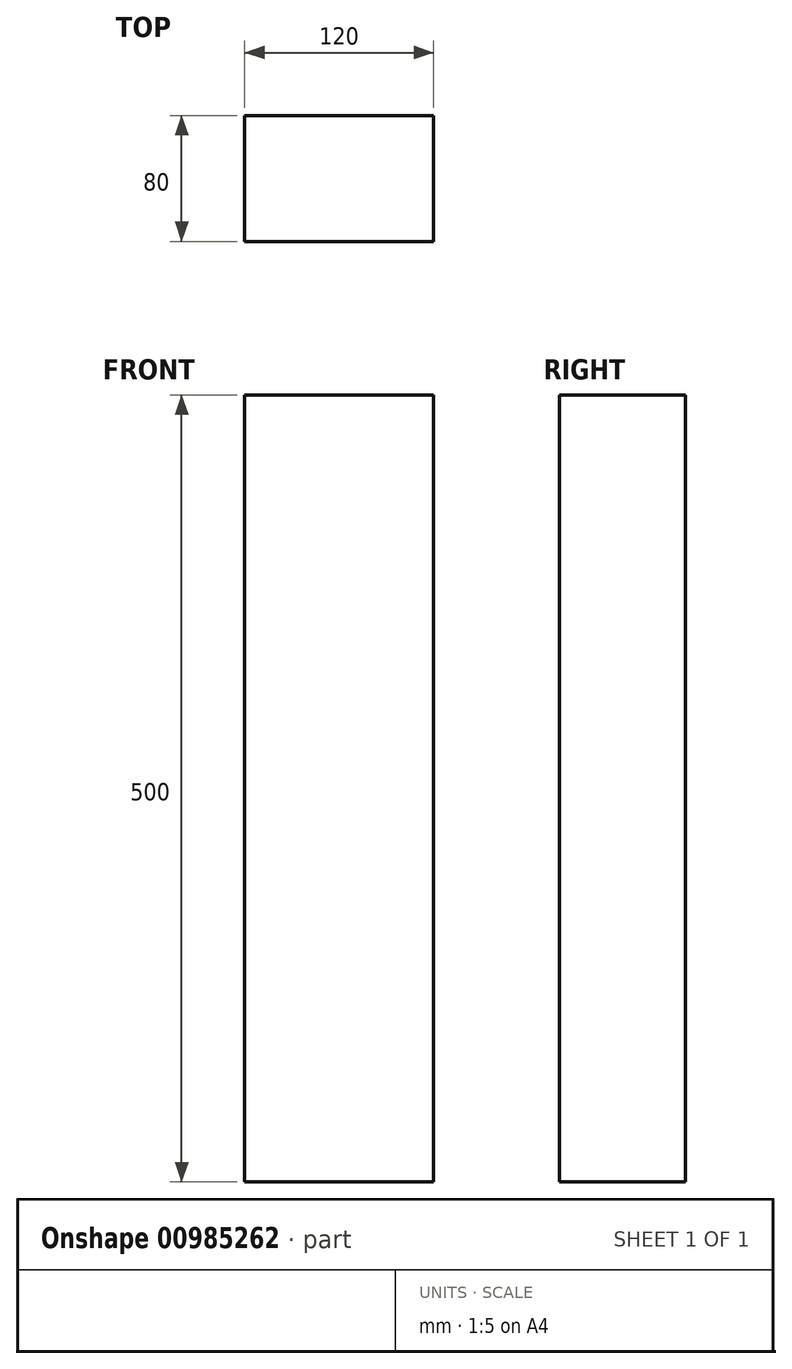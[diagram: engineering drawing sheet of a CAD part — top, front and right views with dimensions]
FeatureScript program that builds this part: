
annotation { "Feature Type Name" : "Feature", "Feature Type Description" : "" }
export const myFeature = defineFeature(function(context is Context, id is Id, definition is map)
    precondition{}
    {
        {
            var Q0;
            Q0=qCreatedBy(makeId("Top.planeOp"),FACE);
            var sketch = newSketch(context, id + "F0", { "sketchPlane" : qUnion([Q0])});
            skLineSegment(sketch, "E0.bottom", {"start": v(0, 0) * mm, "end": v(120, 0) * mm});
            skLineSegment(sketch, "E0.top", {"start": v(0, 80) * mm, "end": v(120, 80) * mm});
            skLineSegment(sketch, "E0.left", {"start": v(0, 0) * mm, "end": v(0, 80) * mm});
            skLineSegment(sketch, "E0.right", {"start": v(120, 0) * mm, "end": v(120, 80) * mm});
            skSolve(sketch);
        }
        {
            var Q0;
            Q0 = qSketchRegion(id + "F0", true);
            extrude(context, id + "F1", {"entities" : qUnion([Q0]), "depth" : 500 * mm, "offsetDistance" : 25 * mm});
        }
    });
